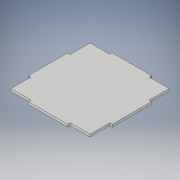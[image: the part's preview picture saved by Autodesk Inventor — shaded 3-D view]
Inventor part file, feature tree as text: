
AUTODESK INVENTOR PART (.ipt)
format: ipt  version: 2019 (Build 230136000, 136)  size: 114,688 bytes
history: native  units: mm
features: other x1, extrude x1, sketch x1
ambient origin geometry x8: Origin, YZ Plane, XZ Plane, XY Plane, X Axis, Y Axis, Z Axis, Center Point
bodies: Body1 (feature_tree)
feature tree (3):
  other  "Sólido1"
  extrude  "Extrusión1"  Depth=100.0mm
  sketch  "Boceto1"  dims[d0=100.0mm d1=100.0mm d2=3.18mm d3=3.18mm d4=50.0mm d5=25.0mm d6=25.0mm d7=25.0mm d8=3.18mm d9=0.0mm]
